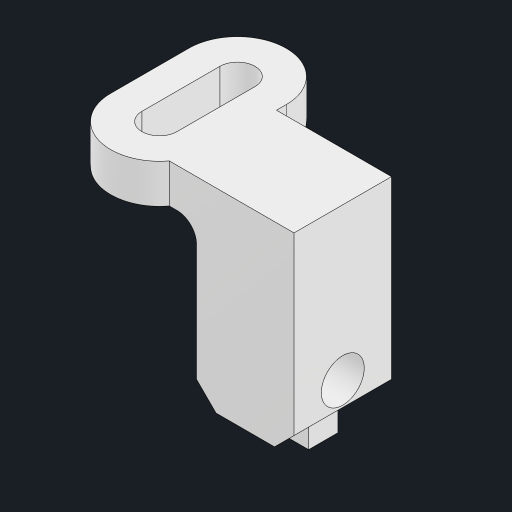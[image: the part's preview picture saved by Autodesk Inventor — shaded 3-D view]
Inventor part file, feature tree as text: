
AUTODESK INVENTOR PART (.ipt)
format: ipt  version: 2023 (Build 270158000, 158)  size: 175,104 bytes
history: native  units: mm
features: sketch x3, extrude x3, other x2, hole x1, fillet x1, chamfer x1
ambient origin geometry x8: Origin, YZ Plane, XZ Plane, XY Plane, X Axis, Y Axis, Z Axis, Center Point
bodies: Body1 (feature_tree)
feature tree (11):
  other  "ソリッド1"
  sketch  "スケッチ1"
  extrude  "押し出し1"  Depth=1.8mm
  extrude  "押し出し4"  Depth=4.0mm
  hole  "穴3"  [1 undecoded]
  fillet  "フィレット3"  Radius=2.0mm
  other  "作業平面2"
  chamfer  "面取り1"  Distance=8.0mm
  extrude  "押し出し5"  Depth=5.0mm
  sketch  "スケッチ6"
  sketch  "スケッチ7"
note: 1 required parameter value undecoded (feature->parameter linkage not recoverable at this tier; creation-order binding heuristic only, values carry confidence <= 0.55)
